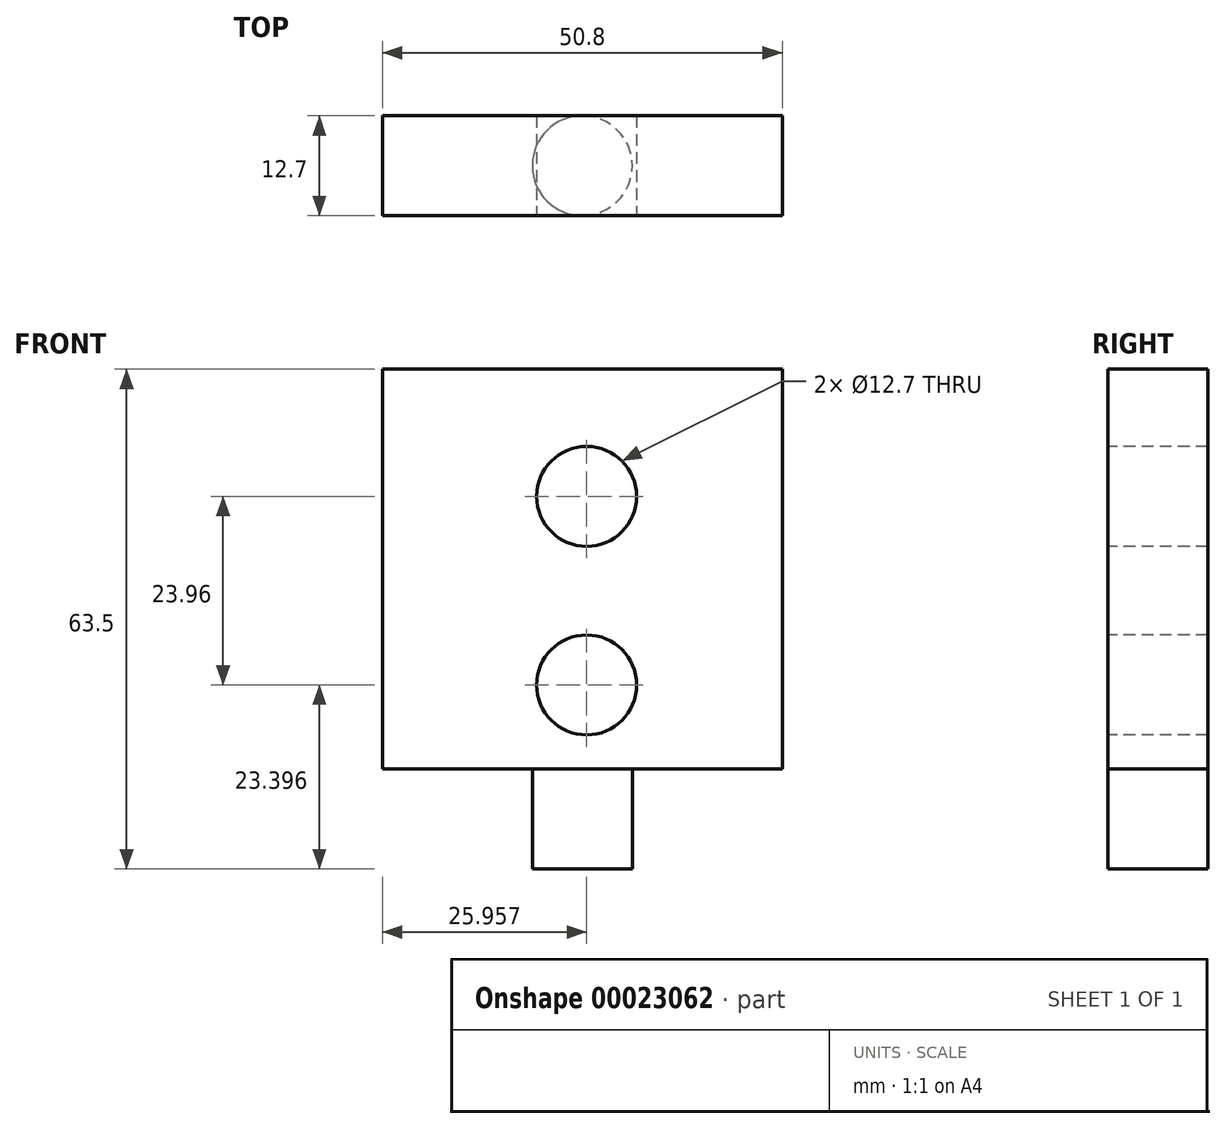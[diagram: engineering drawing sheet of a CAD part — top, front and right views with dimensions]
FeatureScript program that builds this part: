
annotation { "Feature Type Name" : "Feature", "Feature Type Description" : "" }
export const myFeature = defineFeature(function(context is Context, id is Id, definition is map)
    precondition{}
    {
        {
            var Q0;
            Q0=qCreatedBy(makeId("Front.planeOp"),FACE);
            var sketch = newSketch(context, id + "F0", { "sketchPlane" : qUnion([Q0])});
            skLineSegment(sketch, "E0.bottom", {"start": v(0, 0) * mm, "end": v(50.8, 0) * mm});
            skLineSegment(sketch, "E0.top", {"start": v(0, 50.8) * mm, "end": v(50.8, 50.8) * mm});
            skLineSegment(sketch, "E0.left", {"start": v(0, 0) * mm, "end": v(0, 50.8) * mm});
            skLineSegment(sketch, "E0.right", {"start": v(50.8, 0) * mm, "end": v(50.8, 50.8) * mm});
            skSolve(sketch);
        }
        {
            var Q0;
            Q0=makeQuery(id+"F0.imprint","IMPRINT",FACE,{"disambiguationData":[TD([[makeQuery(id+"F0.imprint","IMPRINT",EDGE,{"derivedFrom":sQuery(id+"F0.wireOp",EDGE,"E0.bottom")}),1.0]])]});
            extrude(context, id + "F1", {"entities" : qUnion([Q0]), "depth" : 12.7 * mm});
        }
        {
            var Q0;
            Q0=makeQuery(id+"F1.opExtrude","CAP_FACE",FACE,{"disambiguationData":[OSD([sQuery(id+"F0.wireOp",EDGE,"E0.bottom"),sQuery(id+"F0.wireOp",EDGE,"E0.top"),sQuery(id+"F0.wireOp",EDGE,"E0.left"),sQuery(id+"F0.wireOp",EDGE,"E0.right")])],"isStart":false});
            var sketch = newSketch(context, id + "F2", { "sketchPlane" : qUnion([Q0])});
            skPoint(sketch, "E1", {"position": v(25.96, 10.7) * mm});
            skSolve(sketch);
        }
        {
            var Q0;
            Q0=sQuery(id+"F2.wireOp",VERTEX,"E1");
            var Q1;
            Q1=makeQuery(id+"F1.opExtrude","SWEPT_BODY",BODY,{"disambiguationData":[OSD([sQuery(id+"F0.wireOp",EDGE,"E0.bottom"),sQuery(id+"F0.wireOp",EDGE,"E0.top"),sQuery(id+"F0.wireOp",EDGE,"E0.left"),sQuery(id+"F0.wireOp",EDGE,"E0.right")])]});
            hole(context, id + "F3", {"style" : HoleStyle.SIMPLE, "holeDiameter" : 12.7 * mm, "endStyle" : HoleEndStyle.THROUGH, "locations" : qUnion([Q0]), "scope" : qUnion([Q1])});
        }
        {
            var Q0;
            Q0=makeQuery(id+"F1.opExtrude","CAP_FACE",FACE,{"disambiguationData":[OSD([sQuery(id+"F0.wireOp",EDGE,"E0.bottom"),sQuery(id+"F0.wireOp",EDGE,"E0.top"),sQuery(id+"F0.wireOp",EDGE,"E0.left"),sQuery(id+"F0.wireOp",EDGE,"E0.right")])],"isStart":false});
            var sketch = newSketch(context, id + "F4", { "sketchPlane" : qUnion([Q0])});
            skSolve(sketch);
        }
        {
            var Q0;
            Q0=makeQuery(id+"F4.imprint","IMPRINT",FACE,{"disambiguationData":[TD([[makeQuery(id+"F4.imprint","IMPRINT",EDGE,{"derivedFrom":makeQuery(id+"F1.opExtrude","CAP_EDGE",EDGE,{"disambiguationData":[OSD([sQuery(id+"F0.wireOp",EDGE,"E0.bottom")])],"isStart":false})}),1.0]])]});
            var sketch = newSketch(context, id + "F5", { "sketchPlane" : qUnion([Q0])});
            skPoint(sketch, "E2", {"position": v(25.96, 34.66) * mm});
            skSolve(sketch);
        }
        {
            var Q0;
            Q0=sQuery(id+"F5.wireOp",VERTEX,"E2");
            var Q1;
            Q1=makeQuery(id+"F1.opExtrude","SWEPT_BODY",BODY,{"disambiguationData":[OSD([sQuery(id+"F0.wireOp",EDGE,"E0.bottom"),sQuery(id+"F0.wireOp",EDGE,"E0.top"),sQuery(id+"F0.wireOp",EDGE,"E0.left"),sQuery(id+"F0.wireOp",EDGE,"E0.right")])]});
            hole(context, id + "F6", {"style" : HoleStyle.SIMPLE, "holeDiameter" : 12.7 * mm, "endStyle" : HoleEndStyle.THROUGH, "locations" : qUnion([Q0]), "scope" : qUnion([Q1])});
        }
        {
            var Q0;
            Q0=makeQuery(id+"F1.opExtrude","SWEPT_FACE",FACE,{"disambiguationData":[OSD([sQuery(id+"F0.wireOp",EDGE,"E0.bottom")])]});
            var sketch = newSketch(context, id + "F7", { "sketchPlane" : qUnion([Q0])});
            skPoint(sketch, "E3", {"position": v(25.4, 6.35) * mm});
            skCircle(sketch, "E4", {"center": v(25.4, 6.35) * mm, "radius": 6.35 * mm});
            skPoint(sketch, "E5.orphan", {"position": v(50.8, 6.35) * mm});
            skPoint(sketch, "E6.orphan", {"position": v(0, 6.35) * mm});
            skPoint(sketch, "E7.orphan", {"position": v(25.4, 0) * mm});
            skPoint(sketch, "E8.start.orphan", {"position": v(25.4, 12.7) * mm});
            skSolve(sketch);
        }
        {
            var Q0;
            {var subQ0=sQuery(id+"F7.wireOp",EDGE,"E4");var subQ1=sQuery(id+"F0.wireOp",EDGE,"E0.bottom");var subQ3=makeQuery(id+"F7.imprint","INTERSECT",VERTEX,{"derivedFrom":[makeQuery(id+"F1.opExtrude","CAP_EDGE",EDGE,{"disambiguationData":[OSD([subQ1])],"isStart":true}),subQ0]});Q0=makeQuery(id+"F7.imprint","IMPRINT",FACE,{"disambiguationData":[TD([[makeQuery(id+"F7.imprint","IMPRINT",EDGE,{"disambiguationData":[TD([[subQ3,1.0]])],"derivedFrom":subQ0}),1.0]])]});}
            extrude(context, id + "F8", {"entities" : qUnion([Q0]), "operationType" : NewBodyOperationType.ADD, "depth" : 12.7 * mm});
        }
    });
